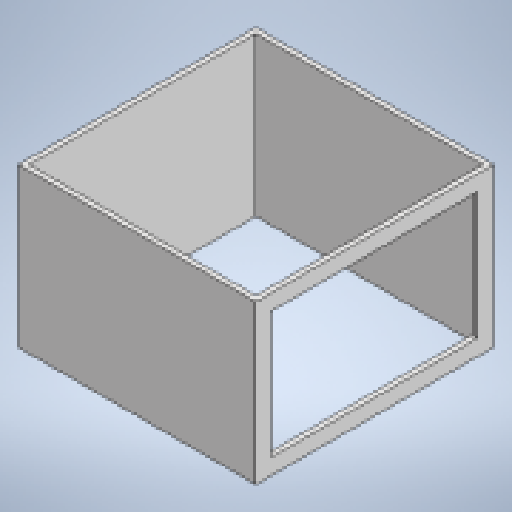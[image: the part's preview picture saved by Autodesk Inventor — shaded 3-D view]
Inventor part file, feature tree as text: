
AUTODESK INVENTOR PART (.ipt)
format: ipt  version: 2025.1 (Build 291241020, 241B)  size: 172,032 bytes
history: native  units: mm
features: extrude x3, sketch x3, projected_geometry x2, shell x1, pattern_linear x1, pattern_circular x1
ambient origin geometry x8: Origin, YZ Plane, XZ Plane, XY Plane, X Axis, Y Axis, Z Axis, Center Point
bodies: Solid1 (feature_tree)
feature tree (11):
  extrude  "Extrusion1"  Depth=500.0mm
  shell  "Shell1"  Thickness=300.0mm
  extrude  "Extrusion2"  Depth=300.0mm
  pattern_linear  "Rectangular Pattern1"  Count1=30  [1 undecoded]
  pattern_circular  "Circular Pattern1"  Count=15  [1 undecoded]
  extrude  "Extrusion3"  Depth=300.0mm
  sketch  "Sketch1"  dims[d0=500.0mm d1=500.0mm d2=300.0mm d3=0.0mm]
  sketch  "Sketch2"  dims[d4=10.0mm d5=60.0mm d6=300.0mm d7=150.0mm]
  projected_geometry  "Projected Loop1"
  sketch  "Sketch3"  dims[d8=60.0mm d9=35.0mm d10=205.0mm d11=50.0mm d12=10.0mm d13=0.0mm d14=30.0mm d16=40.0mm d17=40.0mm d18=360.0deg d20=30.0mm d21=300.0mm d22=0.0mm]
  projected_geometry  "Projected Loop2"
note: 2 required parameter values undecoded (feature->parameter linkage not recoverable at this tier; creation-order binding heuristic only, values carry confidence <= 0.55)
